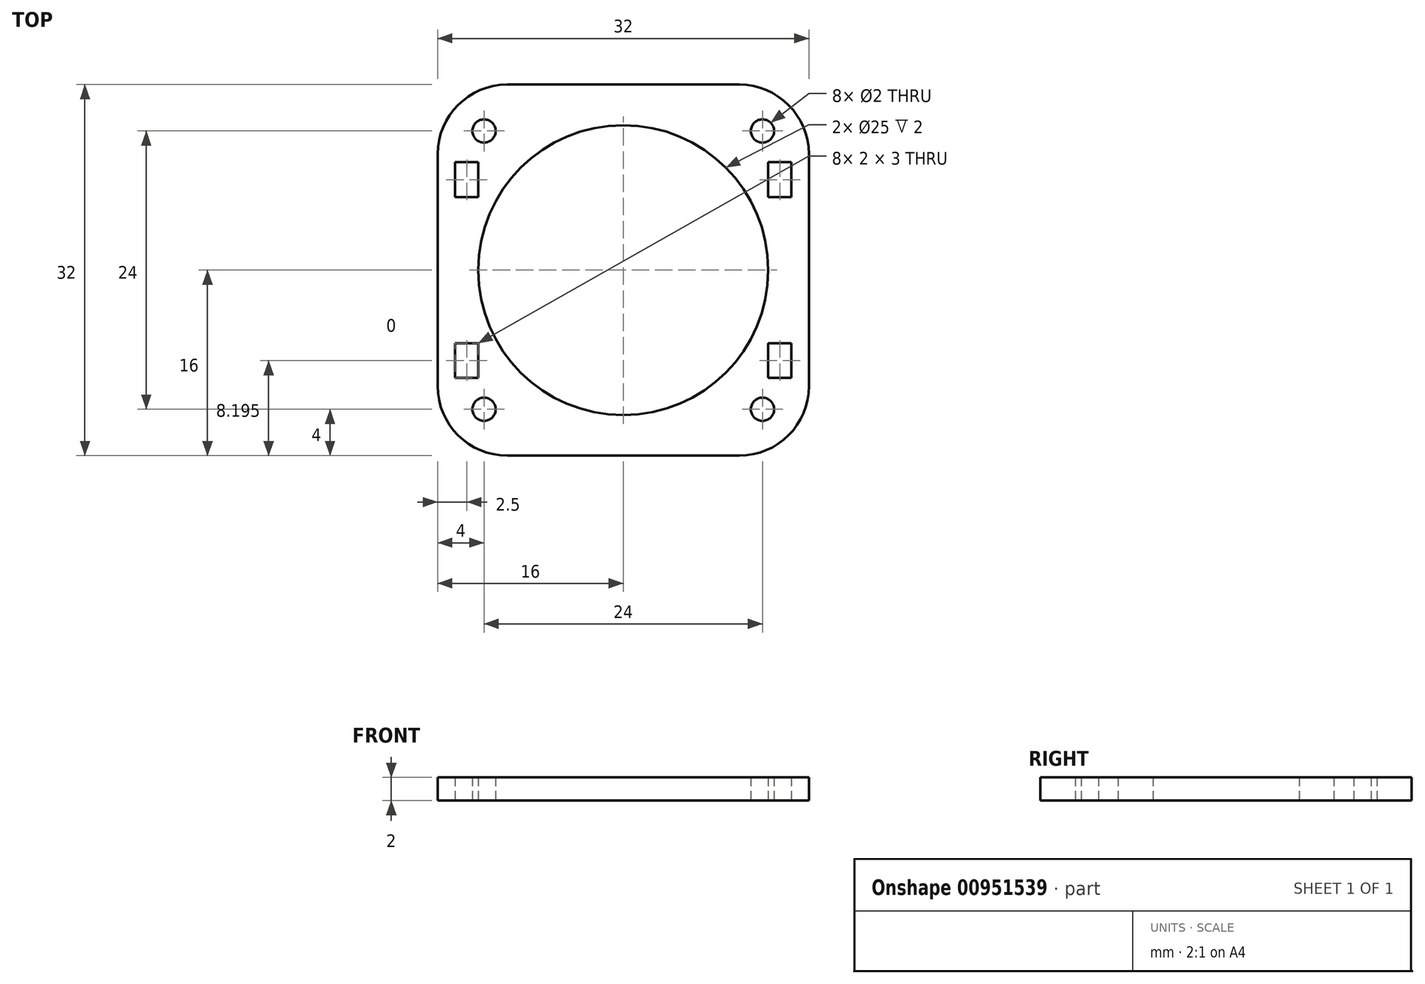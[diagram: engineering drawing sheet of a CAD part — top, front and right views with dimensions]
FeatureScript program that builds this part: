
annotation { "Feature Type Name" : "Feature", "Feature Type Description" : "" }
export const myFeature = defineFeature(function(context is Context, id is Id, definition is map)
    precondition{}
    {
        {
            var Q0;
            Q0=qCreatedBy(makeId("Top.planeOp"),FACE);
            var sketch = newSketch(context, id + "F0", { "sketchPlane" : qUnion([Q0])});
            skLineSegment(sketch, "E0.bottom", {"start": v(-10, 16) * mm, "end": v(10, 16) * mm});
            skLineSegment(sketch, "E0.top", {"start": v(-10, -16) * mm, "end": v(10, -16) * mm});
            skLineSegment(sketch, "E0.left", {"start": v(-16, 10) * mm, "end": v(-16, -10) * mm});
            skLineSegment(sketch, "E0.right", {"start": v(16, 10) * mm, "end": v(16, -10) * mm});
            skPoint(sketch, "E0.middle", {"position": v(0, 0) * mm});
            skCircle(sketch, "E1", {"center": v(0, 0) * mm, "radius": 12.5 * mm});
            skCircle(sketch, "E2", {"center": v(12, 12) * mm, "radius": 1 * mm});
            skCircle(sketch, "E3", {"center": v(-12, 12) * mm, "radius": 1 * mm});
            skCircle(sketch, "E4", {"center": v(-12, -12) * mm, "radius": 1 * mm});
            skCircle(sketch, "E5", {"center": v(12, -12) * mm, "radius": 1 * mm});
            skPoint(sketch, "E6.visualSharp", {"position": v(16, 16) * mm});
            skArc(sketch, "E6.filletArc", {"start": v(16, 10) * mm, "mid": v(14.24, 14.24) * mm, "end": v(10, 16) * mm});
            skPoint(sketch, "E7.visualSharp", {"position": v(16, -16) * mm});
            skArc(sketch, "E7.filletArc", {"start": v(10, -16) * mm, "mid": v(14.24, -14.24) * mm, "end": v(16, -10) * mm});
            skPoint(sketch, "E8.visualSharp", {"position": v(-16, -16) * mm});
            skArc(sketch, "E8.filletArc", {"start": v(-16, -10) * mm, "mid": v(-14.24, -14.24) * mm, "end": v(-10, -16) * mm});
            skPoint(sketch, "E9.visualSharp", {"position": v(-16, 16) * mm});
            skArc(sketch, "E9.filletArc", {"start": v(-10, 16) * mm, "mid": v(-14.24, 14.24) * mm, "end": v(-16, 10) * mm});
            skLineSegment(sketch, "E10.bottom", {"start": v(-14.5, 6.3) * mm, "end": v(-12.5, 6.3) * mm});
            skLineSegment(sketch, "E10.top", {"start": v(-14.5, 9.3) * mm, "end": v(-12.5, 9.3) * mm});
            skLineSegment(sketch, "E10.left", {"start": v(-14.5, 6.3) * mm, "end": v(-14.5, 9.3) * mm});
            skLineSegment(sketch, "E10.right", {"start": v(-12.5, 6.3) * mm, "end": v(-12.5, 9.3) * mm});
            skPoint(sketch, "E10.middle", {"position": v(-13.5, 7.8) * mm});
            skLineSegment(sketch, "E11.bottom", {"start": v(-14.5, -9.3) * mm, "end": v(-12.5, -9.3) * mm});
            skLineSegment(sketch, "E11.top", {"start": v(-14.5, -6.3) * mm, "end": v(-12.5, -6.3) * mm});
            skLineSegment(sketch, "E11.left", {"start": v(-14.5, -9.3) * mm, "end": v(-14.5, -6.3) * mm});
            skLineSegment(sketch, "E11.right", {"start": v(-12.5, -9.3) * mm, "end": v(-12.5, -6.3) * mm});
            skPoint(sketch, "E11.middle", {"position": v(-13.5, -7.8) * mm});
            skLineSegment(sketch, "E12.bottom", {"start": v(12.5, -9.3) * mm, "end": v(14.5, -9.3) * mm});
            skLineSegment(sketch, "E12.top", {"start": v(12.5, -6.3) * mm, "end": v(14.5, -6.3) * mm});
            skLineSegment(sketch, "E12.left", {"start": v(12.5, -9.3) * mm, "end": v(12.5, -6.3) * mm});
            skLineSegment(sketch, "E12.right", {"start": v(14.5, -9.3) * mm, "end": v(14.5, -6.3) * mm});
            skPoint(sketch, "E12.middle", {"position": v(13.5, -7.8) * mm});
            skLineSegment(sketch, "E13.bottom", {"start": v(12.5, 6.3) * mm, "end": v(14.5, 6.3) * mm});
            skLineSegment(sketch, "E13.top", {"start": v(12.5, 9.3) * mm, "end": v(14.5, 9.3) * mm});
            skLineSegment(sketch, "E13.left", {"start": v(12.5, 6.3) * mm, "end": v(12.5, 9.3) * mm});
            skLineSegment(sketch, "E13.right", {"start": v(14.5, 6.3) * mm, "end": v(14.5, 9.3) * mm});
            skPoint(sketch, "E13.middle", {"position": v(13.5, 7.8) * mm});
            skSolve(sketch);
        }
        {
            var Q0;
            Q0 = qSketchRegion(id + "F0", true);
            extrude(context, id + "F1", {"entities" : qUnion([Q0]), "depth" : 2 * mm, "offsetDistance" : 25 * mm});
        }
        {
            var Q0;
            Q0=qSketchRegion(id+"F0",true);
            extrude(context, id + "F2", {"entities" : qUnion([Q0]), "depth" : 2 * mm, "offsetDistance" : 25 * mm});
        }
    });
